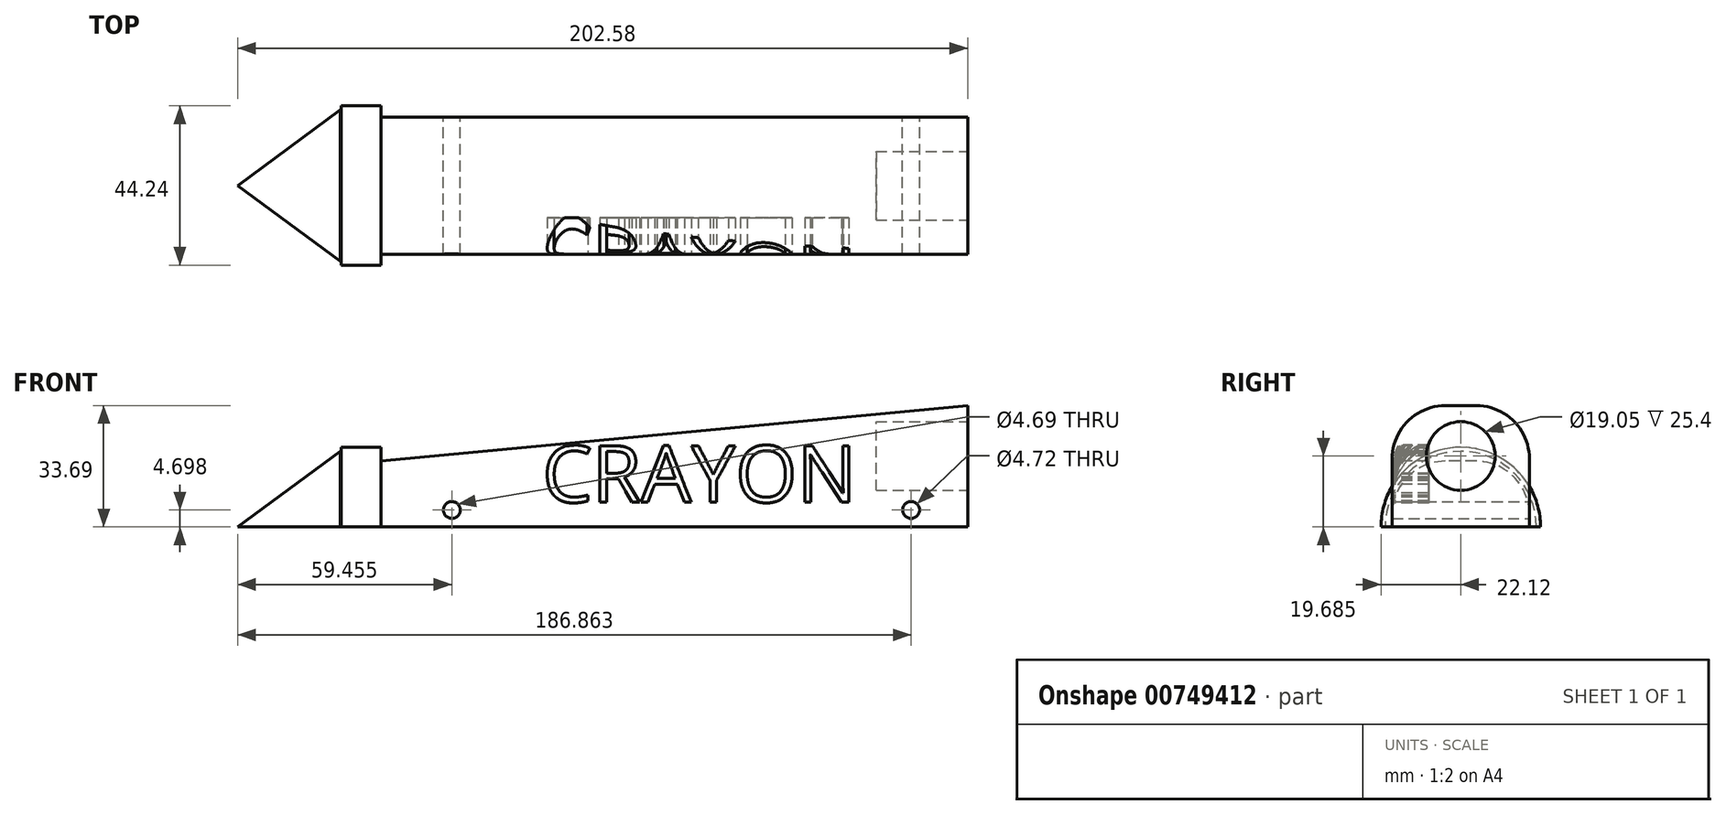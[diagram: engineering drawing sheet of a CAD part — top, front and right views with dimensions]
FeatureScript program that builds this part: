
annotation { "Feature Type Name" : "Feature", "Feature Type Description" : "" }
export const myFeature = defineFeature(function(context is Context, id is Id, definition is map)
    precondition{}
    {
        {
            var Q0;
            Q0=qCreatedBy(makeId("Front.planeOp"),FACE);
            var sketch = newSketch(context, id + "F0", { "sketchPlane" : qUnion([Q0])});
            skLineSegment(sketch, "E0", {"start": v(-74.11, 0) * mm, "end": v(-74.11, 18.03) * mm});
            skLineSegment(sketch, "E1", {"start": v(-74.11, 18.03) * mm, "end": v(90.99, 33.69) * mm});
            skLineSegment(sketch, "E2", {"start": v(90.99, 33.69) * mm, "end": v(90.99, 0) * mm});
            skLineSegment(sketch, "E3", {"start": v(-74.11, 0) * mm, "end": v(90.99, 0) * mm});
            skSolve(sketch);
        }
        {
            var Q0;
            Q0=qCreatedBy(makeId("Front.planeOp"),FACE);
            var sketch = newSketch(context, id + "F1", { "sketchPlane" : qUnion([Q0])});
            skLineSegment(sketch, "E4", {"start": v(-71.77, 22.12) * mm, "end": v(-82.85, 22.12) * mm});
            skLineSegment(sketch, "E5", {"start": v(-82.85, 22.12) * mm, "end": v(-82.85, 0) * mm});
            skLineSegment(sketch, "E6", {"start": v(-82.85, 0) * mm, "end": v(-72.07, 0) * mm});
            skLineSegment(sketch, "E7", {"start": v(-72.07, 0) * mm, "end": v(-71.77, 22.12) * mm});
            skSolve(sketch);
        }
        {
            var Q0;
            Q0=qCreatedBy(makeId("Front.planeOp"),FACE);
            var sketch = newSketch(context, id + "F2", { "sketchPlane" : qUnion([Q0])});
            skLineSegment(sketch, "E8", {"start": v(-83.12, 21) * mm, "end": v(-111.59, 0) * mm});
            skLineSegment(sketch, "E9", {"start": v(-111.59, 0) * mm, "end": v(-82.85, 0) * mm});
            skLineSegment(sketch, "E10", {"start": v(-82.85, 0) * mm, "end": v(-83.12, 21) * mm});
            skSolve(sketch);
        }
        {
            var Q0;
            Q0=makeQuery(id+"F0.imprint","IMPRINT",FACE,{"disambiguationData":[TD([[makeQuery(id+"F0.imprint","IMPRINT",EDGE,{"derivedFrom":sQuery(id+"F0.wireOp",EDGE,"E0")}),-1.0]])]});
            extrude(context, id + "F3", {"entities" : qUnion([Q0]), "depth" : 19.05 * mm, "offsetDistance" : 25.4 * mm, "hasSecondDirection" : true, "secondDirectionOppositeDirection" : true, "secondDirectionDepth" : 19.05 * mm});
        }
        {
            var Q0;
            Q0=makeQuery(id+"F3.opExtrude","CAP_EDGE",EDGE,{"disambiguationData":[OSD([sQuery(id+"F0.wireOp",EDGE,"E1")])],"isStart":false});
            var Q1;
            Q1=makeQuery(id+"F3.opExtrude","CAP_EDGE",EDGE,{"disambiguationData":[OSD([sQuery(id+"F0.wireOp",EDGE,"E1")])],"isStart":true});
            fillet(context, id + "F4", {"entities" : qUnion([Q0, Q1]), "radius" : 14.72 * mm, "tangentPropagation" : true, "allowEdgeOverflow" : false});
        }
        {
            var Q0;
            Q0=qCreatedBy(makeId("Front.planeOp"),FACE);
            var sketch = newSketch(context, id + "F5", { "sketchPlane" : qUnion([Q0])});
            skLineSegment(sketch, "E11.bottom", {"start": v(-114.87, 0) * mm, "end": v(106.23, 0) * mm});
            skLineSegment(sketch, "E11.top", {"start": v(-114.87, 0) * mm, "end": v(106.23, 0) * mm});
            skLineSegment(sketch, "E11.left", {"start": v(-114.87, 0) * mm, "end": v(-114.87, 0) * mm});
            skLineSegment(sketch, "E11.right", {"start": v(106.23, 0) * mm, "end": v(106.23, 0) * mm});
            skLineSegment(sketch, "E12.bottom", {"start": v(105.4, -25.89) * mm, "end": v(-114.87, -25.89) * mm});
            skLineSegment(sketch, "E12.top", {"start": v(105.4, 0) * mm, "end": v(-114.87, 0) * mm});
            skLineSegment(sketch, "E12.left", {"start": v(105.4, -25.89) * mm, "end": v(105.4, 0) * mm});
            skLineSegment(sketch, "E12.right", {"start": v(-114.87, -25.89) * mm, "end": v(-114.87, 0) * mm});
            skSolve(sketch);
        }
        {
            var Q0;
            Q0=makeQuery(id+"F3.opExtrude","CAP_FACE",FACE,{"disambiguationData":[OSD([sQuery(id+"F0.wireOp",EDGE,"E0"),sQuery(id+"F0.wireOp",EDGE,"E1"),sQuery(id+"F0.wireOp",EDGE,"E2"),sQuery(id+"F0.wireOp",EDGE,"E3")])],"isStart":false});
            var sketch = newSketch(context, id + "F6", { "sketchPlane" : qUnion([Q0])});
            skText(sketch, "E13", { "text": "CRAYON", "fontName": "OpenSans-Regular.ttf"});
            const initialGuessF6  = {"E13": [-0.02703, 0.00685, 1, 0, 0.0158]};
            skSetInitialGuess(sketch, initialGuessF6);
            skSolve(sketch);
        }
        {
            var Q0;
            Q0 = qSketchRegion(id + "F6", true);
            extrude(context, id + "F7", {"entities" : qUnion([Q0]), "operationType" : NewBodyOperationType.REMOVE, "oppositeDirection" : true, "depth" : 10.16 * mm, "offsetDistance" : 25.4 * mm});
        }
        {
            var Q0;
            Q0=qCreatedBy(makeId("Front.planeOp"),FACE);
            var sketch = newSketch(context, id + "F8", { "sketchPlane" : qUnion([Q0])});
            skCircle(sketch, "E14", {"center": v(-52.13, 4.7) * mm, "radius": 2.35 * mm});
            skCircle(sketch, "E15", {"center": v(75.27, 4.7) * mm, "radius": 2.36 * mm});
            skSolve(sketch);
        }
        {
            var Q0;
            Q0 = qSketchRegion(id + "F8", true);
            extrude(context, id + "F9", {"entities" : qUnion([Q0]), "operationType" : NewBodyOperationType.REMOVE, "depth" : 25.4 * mm, "offsetDistance" : 25.4 * mm, "hasSecondDirection" : true, "secondDirectionOppositeDirection" : true, "secondDirectionDepth" : 25.4 * mm});
        }
        {
            var Q0;
            Q0=makeQuery(id+"F3.opExtrude","SWEPT_FACE",FACE,{"disambiguationData":[OSD([sQuery(id+"F0.wireOp",EDGE,"E2")])]});
            var sketch = newSketch(context, id + "F10", { "sketchPlane" : qUnion([Q0])});
            skCircle(sketch, "E16", {"center": v(0, 19.68) * mm, "radius": 9.53 * mm});
            skSolve(sketch);
        }
        {
            var Q0;
            Q0=makeQuery(id+"F10.imprint","IMPRINT",FACE,{"disambiguationData":[TD([[makeQuery(id+"F10.imprint","IMPRINT",EDGE,{"derivedFrom":sQuery(id+"F10.wireOp",EDGE,"E16")}),1.0]])]});
            var Q1;
            Q1=sQuery(id+"F10.wireOp",EDGE,"E16");
            extrude(context, id + "F11", {"entities" : qUnion([Q0]), "operationType" : NewBodyOperationType.REMOVE, "surfaceEntities" : qUnion([Q1]), "oppositeDirection" : true, "depth" : 25.4 * mm, "offsetDistance" : 25.4 * mm});
        }
        {
            var Q0;
            Q0 = qSketchRegion(id + "F5", true);
            extrude(context, id + "F12", {"entities" : qUnion([Q0]), "operationType" : NewBodyOperationType.REMOVE, "oppositeDirection" : true, "depth" : 25.4 * mm, "offsetDistance" : 25.4 * mm, "hasSecondDirection" : true, "secondDirectionOppositeDirection" : false, "secondDirectionDepth" : 25.4 * mm});
        }
        {
            var Q0;
            Q0=makeQuery(id+"F2.imprint","IMPRINT",FACE,{"disambiguationData":[TD([[makeQuery(id+"F2.imprint","IMPRINT",EDGE,{"derivedFrom":sQuery(id+"F2.wireOp",EDGE,"E8")}),1.0]])]});
            var Q1;
            Q1=sQuery(id+"F2.wireOp",EDGE,"E9");
            revolve(context, id + "F13", {"surfaceOperationType" : NewSurfaceOperationType.NEW, "entities" : qUnion([Q0]), "axis" : qUnion([Q1]), "revolveType" : RevolveType.TWO_DIRECTIONS, "angle" : 90 * degree, "angleBack" : 270 * degree});
        }
        {
            var Q0;
            Q0=makeQuery(id+"F1.imprint","IMPRINT",FACE,{"disambiguationData":[TD([[makeQuery(id+"F1.imprint","IMPRINT",EDGE,{"derivedFrom":sQuery(id+"F1.wireOp",EDGE,"E4")}),1.0]])]});
            var Q1;
            Q1=sQuery(id+"F1.wireOp",EDGE,"E6");
            revolve(context, id + "F14", {"operationType" : NewBodyOperationType.ADD, "surfaceOperationType" : NewSurfaceOperationType.NEW, "entities" : qUnion([Q0]), "axis" : qUnion([Q1]), "revolveType" : RevolveType.TWO_DIRECTIONS, "angle" : 90 * degree, "angleBack" : 270 * degree});
        }
    });
